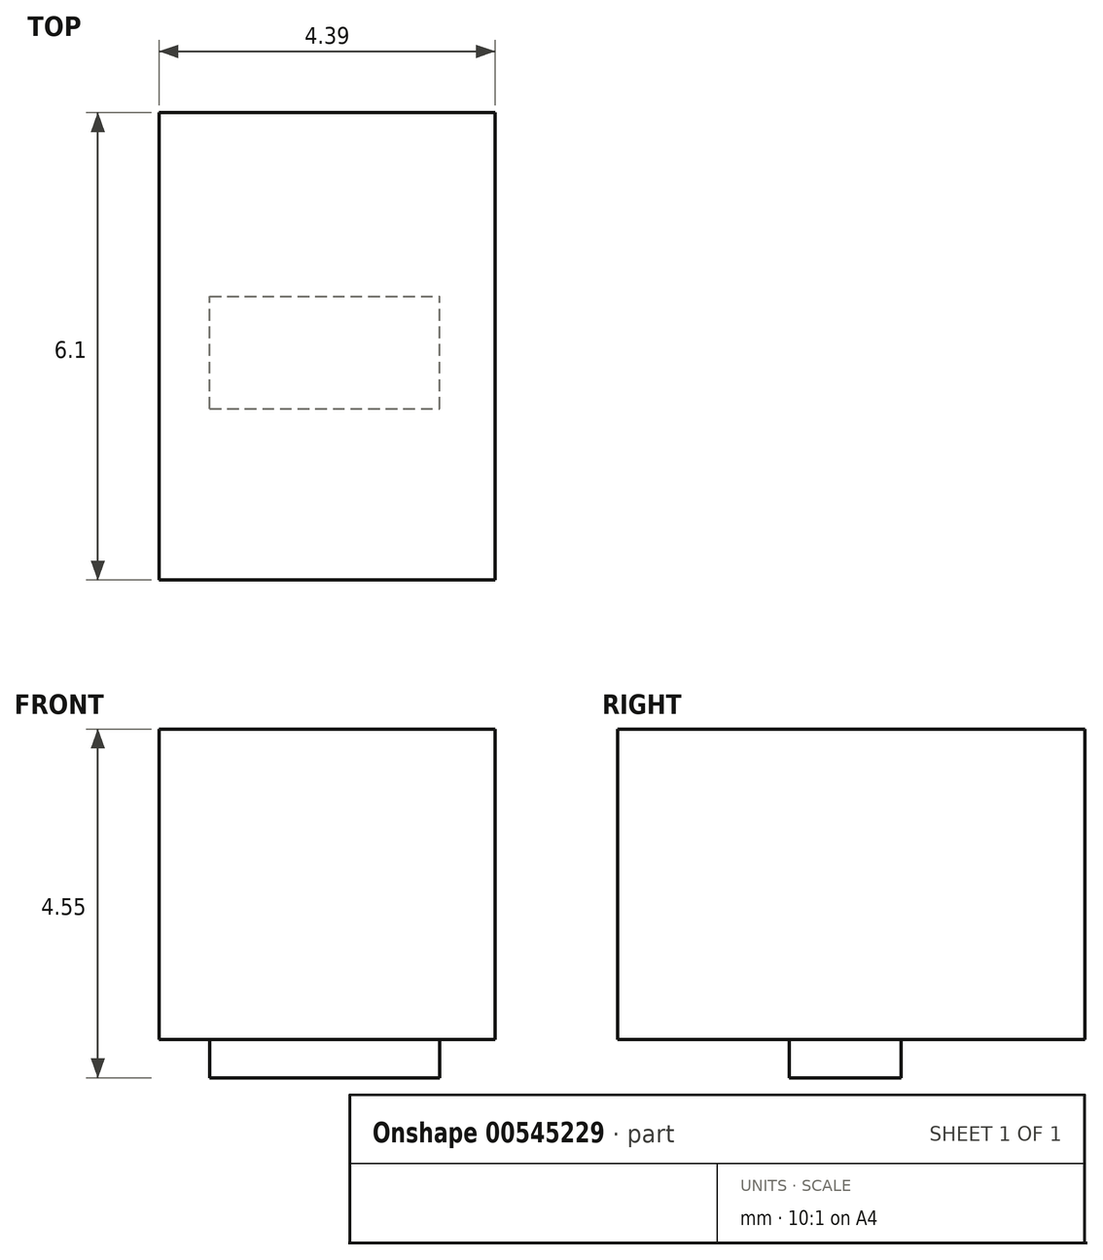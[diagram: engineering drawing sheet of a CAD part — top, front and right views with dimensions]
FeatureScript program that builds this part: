
annotation { "Feature Type Name" : "Feature", "Feature Type Description" : "" }
export const myFeature = defineFeature(function(context is Context, id is Id, definition is map)
    precondition{}
    {
        {
            var Q0;
            Q0=qCreatedBy(makeId("Front.planeOp"),FACE);
            var sketch = newSketch(context, id + "F0", { "sketchPlane" : qUnion([Q0])});
            skLineSegment(sketch, "E0.bottom", {"start": v(-4.39, 0) * mm, "end": v(0, 0) * mm});
            skLineSegment(sketch, "E0.top", {"start": v(-4.39, -4.05) * mm, "end": v(0, -4.05) * mm});
            skLineSegment(sketch, "E0.left", {"start": v(-4.39, 0) * mm, "end": v(-4.39, -4.05) * mm});
            skLineSegment(sketch, "E0.right", {"start": v(0, 0) * mm, "end": v(0, -4.05) * mm});
            skSolve(sketch);
        }
        {
            var Q0;
            Q0=makeQuery(id+"F0.imprint","IMPRINT",FACE,{"disambiguationData":[TD([[makeQuery(id+"F0.imprint","IMPRINT",EDGE,{"derivedFrom":sQuery(id+"F0.wireOp",EDGE,"E0.bottom")}),-1.0]])]});
            extrude(context, id + "F1", {"entities" : qUnion([Q0]), "depth" : 6.1 * mm, "offsetDistance" : 25.4 * mm});
        }
        {
            var Q0;
            Q0=makeQuery(id+"F1.opExtrude","SWEPT_FACE",FACE,{"disambiguationData":[OSD([sQuery(id+"F0.wireOp",EDGE,"E0.top")])]});
            var sketch = newSketch(context, id + "F2", { "sketchPlane" : qUnion([Q0])});
            skLineSegment(sketch, "E1.bottom", {"start": v(-3.73, 3.86) * mm, "end": v(-0.73, 3.86) * mm});
            skLineSegment(sketch, "E1.top", {"start": v(-3.73, 2.4) * mm, "end": v(-0.73, 2.4) * mm});
            skLineSegment(sketch, "E1.left", {"start": v(-3.73, 3.86) * mm, "end": v(-3.73, 2.4) * mm});
            skLineSegment(sketch, "E1.right", {"start": v(-0.73, 3.86) * mm, "end": v(-0.73, 2.4) * mm});
            skSolve(sketch);
        }
        {
            var Q0;
            Q0=makeQuery(id+"F2.imprint","IMPRINT",FACE,{"disambiguationData":[TD([[makeQuery(id+"F2.imprint","IMPRINT",EDGE,{"derivedFrom":sQuery(id+"F2.wireOp",EDGE,"E1.bottom")}),-1.0]])]});
            extrude(context, id + "F3", {"entities" : qUnion([Q0]), "operationType" : NewBodyOperationType.ADD, "depth" : 0.5 * mm, "offsetDistance" : 25.4 * mm});
        }
    });
